# Revit family: Furniture_Mirrors_Svedholm_Orbit
name_source: partatom
category: Furniture
revit_build: Autodesk Revit 2018 (Build: 20190510_1515(x64)
units: mm (PartAtom-declared; Revit-internal decimal feet)

## family parameters
Cut with Voids When Loaded = No
Host = Face
OmniClass Number = 23.21.37.13.15
OmniClass Title = Mirrors
Room Calculation Point = No
Shared = No

## types (1)
- ART - (123.600.001)
    BIMobject category = Mirrors
    Default Elevation = 1219 mm
    Description = A mirror with frame in powder coated wire.
    Design country = Sweden
    Edition number = 1
    IFC Classification = Object
    Manufacturer = Svedholm
    Manufacturer country = Sweden
    Manufacturer name = Svedholm
    Masterformat 2014 Code = 08 83 00
    Masterformat 2014 Description = Mirrors
    Material main = Mirror Glass
    Material secondary = Powder coated steel
    Mirror material = Svedholm - Glass - Mirror
    Model = Orbit
    NBS Reference Code = 71-55
    NBS Reference Description = Mirrors
    OmniClass Code = 23-21 37 13 15
    OmniClass Description = Mirrors
    Product Guid = c76ef174-ab7e-446a-bb7d-9d3305f6767f
    Product SKU = Orbit
    Product data url = https://bimobject.com
    Product family = Orbit
    Product group = Mirrors
    Product name = Orbit
    Product url = https://www.svedholm.se
    QR code = https://bimobject.com
    URL = https://www.svedholm.se
    Uniclass 1.4 Code = L8732
    Uniclass 1.4 Description = Mirrors
    Uniclass 2.0 Code = PR-71-55
    Uniclass 2.0 Description = Mirrors
    Uniclass 2015 Code = Pr_25_71_53
    Uniclass 2015 Name = Mirrors

## geometry (parser evidence)
native form markers: Sweep x1
no freeform markers — native parametric forms only
